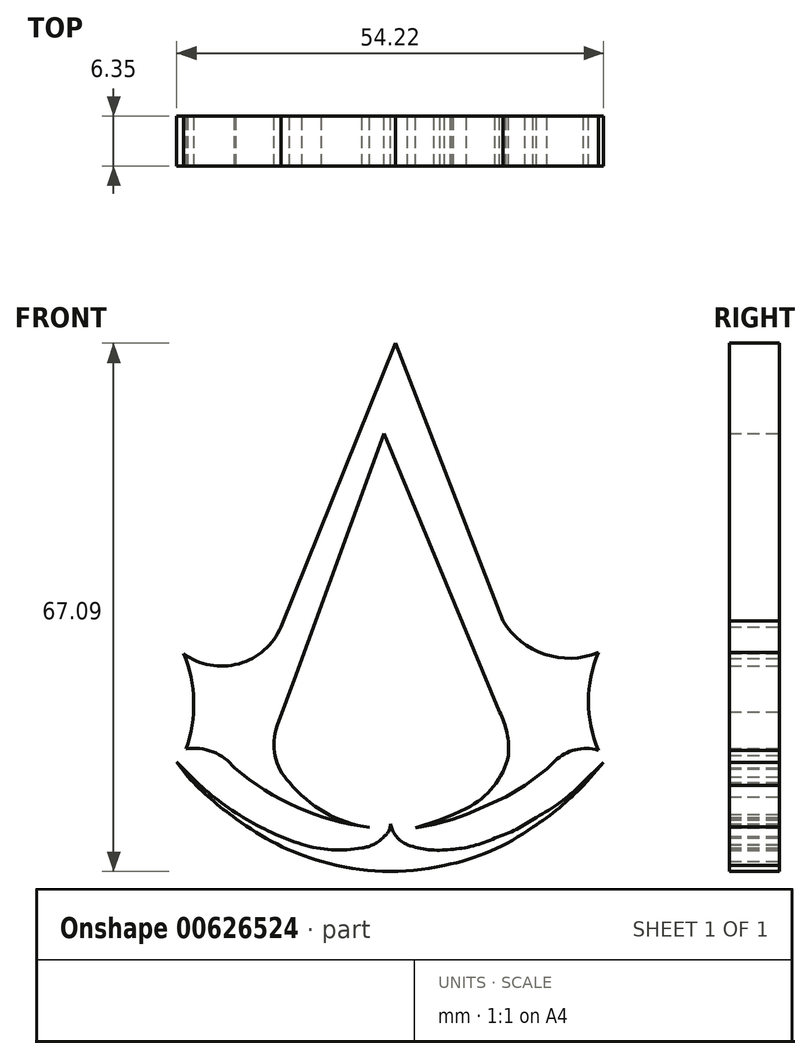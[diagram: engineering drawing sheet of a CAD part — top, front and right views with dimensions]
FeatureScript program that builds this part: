
annotation { "Feature Type Name" : "Feature", "Feature Type Description" : "" }
export const myFeature = defineFeature(function(context is Context, id is Id, definition is map)
    precondition{}
    {
        {
            var Q0;
            Q0=qCreatedBy(makeId("Front.planeOp"),FACE);
            var sketch = newSketch(context, id + "F0", { "sketchPlane" : qUnion([Q0])});
            skArc(sketch, "E0", {"start": v(-26.82, -6.7) * mm, "mid": v(-25.84, -0.6) * mm, "end": v(-27.12, 5.44) * mm});
            skArc(sketch, "E1", {"start": v(-27.12, 5.44) * mm, "mid": v(-20.1, 4.16) * mm, "end": v(-14.75, 8.86) * mm});
            skLineSegment(sketch, "E2", {"start": v(-14.75, 8.86) * mm, "end": v(-0.22, 44.87) * mm});
            skPoint(sketch, "E2.endSnap0", {"position": v(-0.22, 45.85) * mm});
            skLineSegment(sketch, "E3", {"start": v(-0.22, 44.87) * mm, "end": v(13.42, 9.6) * mm});
            skArc(sketch, "E4", {"start": v(13.42, 9.6) * mm, "mid": v(18.75, 5.35) * mm, "end": v(25.57, 5.57) * mm});
            skArc(sketch, "E5", {"start": v(25.57, 5.57) * mm, "mid": v(24.31, -0.63) * mm, "end": v(25.57, -6.83) * mm});
            skArc(sketch, "E6", {"start": v(25.57, -6.83) * mm, "mid": v(22.6, -6.78) * mm, "end": v(20.02, -8.21) * mm});
            skLineSegment(sketch, "E7", {"start": v(20.02, -8.21) * mm, "end": v(19, -9.19) * mm});
            skLineSegment(sketch, "E8", {"start": v(19, -9.19) * mm, "end": v(16.2, -11.32) * mm});
            skLineSegment(sketch, "E9", {"start": v(16.2, -11.32) * mm, "end": v(13.8, -12.74) * mm});
            skLineSegment(sketch, "E10", {"start": v(13.8, -12.74) * mm, "end": v(8.81, -15.01) * mm});
            skLineSegment(sketch, "E11", {"start": v(8.81, -15.01) * mm, "end": v(7.04, -15.6) * mm});
            skLineSegment(sketch, "E12", {"start": v(7.04, -15.6) * mm, "end": v(4.7, -16.22) * mm});
            skLineSegment(sketch, "E13", {"start": v(4.7, -16.22) * mm, "end": v(2.32, -16.71) * mm});
            skLineSegment(sketch, "E14", {"start": v(2.32, -16.71) * mm, "end": v(5.46, -15.7) * mm});
            skLineSegment(sketch, "E15", {"start": v(5.46, -15.7) * mm, "end": v(7.15, -15.01) * mm});
            skLineSegment(sketch, "E16", {"start": v(7.15, -15.01) * mm, "end": v(8.81, -14.2) * mm});
            skArc(sketch, "E17", {"start": v(8.81, -14.2) * mm, "mid": v(12.24, -11.46) * mm, "end": v(14.15, -7.5) * mm});
            skArc(sketch, "E18", {"start": v(14.15, -7.5) * mm, "mid": v(13.95, -4.65) * mm, "end": v(13.02, -1.95) * mm});
            skLineSegment(sketch, "E19", {"start": v(13.02, -1.95) * mm, "end": v(-1.68, 33.43) * mm});
            skLineSegment(sketch, "E20", {"start": v(-1.68, 33.43) * mm, "end": v(-12.87, 2.74) * mm});
            skLineSegment(sketch, "E21", {"start": v(-12.87, 2.74) * mm, "end": v(-15.23, -3.75) * mm});
            skArc(sketch, "E22", {"start": v(-15.23, -3.75) * mm, "mid": v(-15.5, -7.55) * mm, "end": v(-13.7, -10.9) * mm});
            skArc(sketch, "E23", {"start": v(-13.7, -10.9) * mm, "mid": v(-9.15, -14.73) * mm, "end": v(-3.53, -16.65) * mm});
            skArc(sketch, "E24", {"start": v(-20.66, -9.1) * mm, "mid": v(-12.64, -14.1) * mm, "end": v(-3.53, -16.65) * mm});
            skArc(sketch, "E25", {"start": v(-20.66, -9.1) * mm, "mid": v(-23.4, -7.04) * mm, "end": v(-26.82, -6.7) * mm});
            skArc(sketch, "E26", {"start": v(-1.68, -17.8) * mm, "mid": v(-1.06, -17.1) * mm, "end": v(-0.84, -16.2) * mm});
            skArc(sketch, "E27", {"start": v(-4.46, -19.25) * mm, "mid": v(-2.94, -18.78) * mm, "end": v(-1.68, -17.8) * mm});
            skArc(sketch, "E28", {"start": v(-12.1, -18.8) * mm, "mid": v(-8.3, -19.47) * mm, "end": v(-4.46, -19.25) * mm});
            skArc(sketch, "E29", {"start": v(-19.56, -15.36) * mm, "mid": v(-15.93, -17.28) * mm, "end": v(-12.1, -18.8) * mm});
            skArc(sketch, "E30", {"start": v(-26.38, -9.98) * mm, "mid": v(-23.14, -12.88) * mm, "end": v(-19.56, -15.36) * mm});
            skLineSegment(sketch, "E31", {"start": v(-26.38, -9.98) * mm, "end": v(-28, -8.33) * mm});
            skLineSegment(sketch, "E32", {"start": v(-28, -8.33) * mm, "end": v(-26.58, -10.22) * mm});
            skArc(sketch, "E33", {"start": v(-26.58, -10.22) * mm, "mid": v(-23.66, -13.03) * mm, "end": v(-20.45, -15.53) * mm});
            skArc(sketch, "E34", {"start": v(-20.45, -15.53) * mm, "mid": v(-15.28, -18.75) * mm, "end": v(-9.6, -20.96) * mm});
            skArc(sketch, "E35", {"start": v(-9.6, -20.96) * mm, "mid": v(-1.83, -22.2) * mm, "end": v(6, -21.45) * mm});
            skArc(sketch, "E36", {"start": v(6, -21.45) * mm, "mid": v(11.9, -19.64) * mm, "end": v(17.24, -16.59) * mm});
            skArc(sketch, "E37", {"start": v(17.24, -16.59) * mm, "mid": v(20.61, -14.13) * mm, "end": v(23.66, -11.29) * mm});
            skLineSegment(sketch, "E38", {"start": v(23.66, -11.29) * mm, "end": v(26.22, -8.39) * mm});
            skLineSegment(sketch, "E39", {"start": v(26.22, -8.39) * mm, "end": v(23.43, -11.13) * mm});
            skArc(sketch, "E40", {"start": v(17.68, -15.35) * mm, "mid": v(20.7, -13.44) * mm, "end": v(23.43, -11.13) * mm});
            skArc(sketch, "E41", {"start": v(12.44, -17.97) * mm, "mid": v(15.16, -16.87) * mm, "end": v(17.68, -15.35) * mm});
            skArc(sketch, "E42", {"start": v(6.76, -19.42) * mm, "mid": v(9.68, -18.98) * mm, "end": v(12.44, -17.97) * mm});
            skArc(sketch, "E43", {"start": v(1.33, -18.84) * mm, "mid": v(4, -19.47) * mm, "end": v(6.76, -19.42) * mm});
            skArc(sketch, "E44", {"start": v(-0.84, -16.2) * mm, "mid": v(-0.1, -17.8) * mm, "end": v(1.33, -18.84) * mm});
            skSolve(sketch);
        }
        {
            var Q0;
            Q0 = qSketchRegion(id + "F0", true);
            extrude(context, id + "F1", {"entities" : qUnion([Q0]), "depth" : 6.35 * mm, "offsetDistance" : 25.4 * mm});
        }
    });
